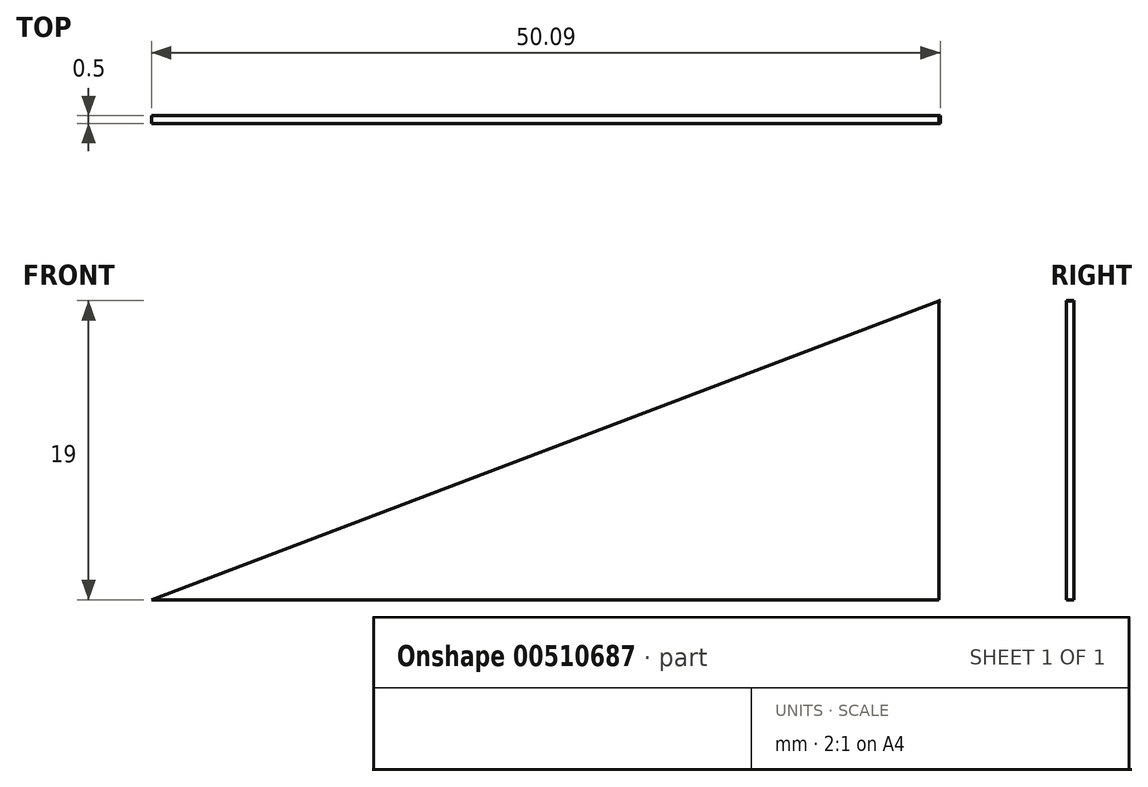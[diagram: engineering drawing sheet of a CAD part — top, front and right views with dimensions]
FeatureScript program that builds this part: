
annotation { "Feature Type Name" : "Feature", "Feature Type Description" : "" }
export const myFeature = defineFeature(function(context is Context, id is Id, definition is map)
    precondition{}
    {
        {
            var Q0;
            Q0=qCreatedBy(makeId("Front.planeOp"),FACE);
            var sketch = newSketch(context, id + "F0", { "sketchPlane" : qUnion([Q0])});
            skLineSegment(sketch, "E0.bottom", {"start": v(-50, 0) * mm, "end": v(0, 0) * mm});
            skLineSegment(sketch, "E0.top", {"start": v(0, 19) * mm, "end": v(0.09, 19) * mm});
            skLineSegment(sketch, "E0.left", {"start": v(-50, 0) * mm, "end": v(-50, 0) * mm});
            skLineSegment(sketch, "E0.right", {"start": v(0, 0) * mm, "end": v(0, 19) * mm});
            skLineSegment(sketch, "E1", {"start": v(-50, 0) * mm, "end": v(0.09, 19) * mm});
            skSolve(sketch);
        }
        {
            var Q0;
            Q0 = qSketchRegion(id + "F4fwhphE2POrpvI_0", true);
            var Q1;
            Q1 = qSketchRegion(id + "F0", true);
            extrude(context, id + "F1", {"entities" : qUnion([Q0, Q1]), "depth" : 0.5 * mm, "offsetDistance" : 25 * mm});
        }
    });
